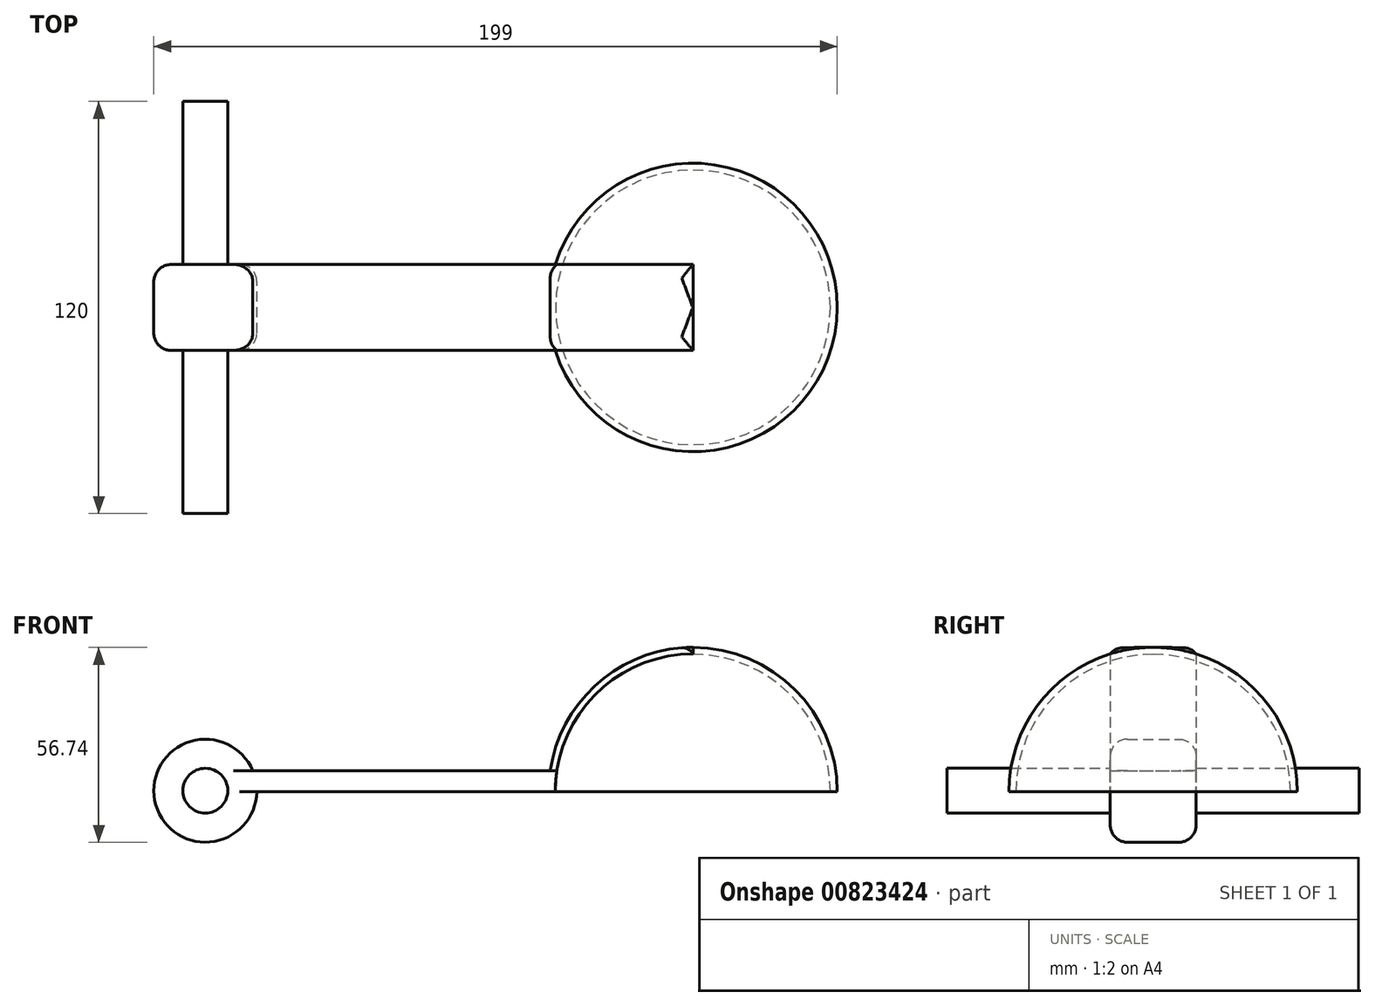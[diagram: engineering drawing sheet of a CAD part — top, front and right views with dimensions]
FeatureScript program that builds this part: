
annotation { "Feature Type Name" : "Feature", "Feature Type Description" : "" }
export const myFeature = defineFeature(function(context is Context, id is Id, definition is map)
    precondition{}
    {
        {
            var Q0;
            Q0=qCreatedBy(makeId("Front.planeOp"),FACE);
            var sketch = newSketch(context, id + "F0", { "sketchPlane" : qUnion([Q0])});
            skLineSegment(sketch, "E0", {"start": v(-42, 0) * mm, "end": v(-40, 0) * mm});
            skLineSegment(sketch, "E1", {"start": v(0, 0) * mm, "end": v(0, 40) * mm});
            skArc(sketch, "E2", {"start": v(-40, 0) * mm, "mid": v(-28.28, 28.28) * mm, "end": v(0, 40) * mm});
            skArc(sketch, "E3.0", {"start": v(-42, 0) * mm, "mid": v(-29.7, 29.7) * mm, "end": v(0, 42) * mm});
            skLineSegment(sketch, "E4", {"start": v(0, 42) * mm, "end": v(0, 40) * mm});
            skPoint(sketch, "E5", {"position": v(0, 20) * mm});
            skPoint(sketch, "E6", {"position": v(-36.93, 20) * mm});
            skPoint(sketch, "E7", {"position": v(-46.93, 20) * mm});
            skArc(sketch, "E8", {"start": v(-36.93, 20) * mm, "mid": v(-36.11, 21.44) * mm, "end": v(-35.24, 22.85) * mm});
            skLineSegment(sketch, "E9", {"start": v(-42, 0) * mm, "end": v(-142, 0) * mm});
            skCircle(sketch, "E10", {"center": v(-142, 0.26) * mm, "radius": 15 * mm});
            skLineSegment(sketch, "E11", {"start": v(-142, 6.07) * mm, "end": v(-41.56, 6.07) * mm});
            skCircle(sketch, "E12", {"center": v(-142, 0.26) * mm, "radius": 6.52 * mm});
            skSolve(sketch);
        }
        {
            var Q0;
            Q0=makeQuery(id+"F0.imprint","IMPRINT",FACE,{"disambiguationData":[TD([[makeQuery(id+"F0.imprint","IMPRINT",EDGE,{"derivedFrom":sQuery(id+"F0.wireOp",EDGE,"E0")}),1.0]])]});
            var Q1;
            Q1=sQuery(id+"F0.wireOp",EDGE,"E1");
            revolve(context, id + "F1", {"entities" : qUnion([Q0]), "axis" : qUnion([Q1]), "revolveType" : RevolveType.FULL, "surfaceOperationType" : NewSurfaceOperationType.NEW});
        }
        {
            var Q0;
            Q0 = qSketchRegion(id + "F0", true);
            extrude(context, id + "F2", {"entities" : qUnion([Q0]), "operationType" : NewBodyOperationType.ADD, "endBound" : BoundingType.SYMMETRIC, "depth" : 25 * mm, "offsetDistance" : 25 * mm});
        }
        {
            var Q0;
            {var subQ0=sQuery(id+"F0.wireOp",EDGE,"E12");var subQ1=makeQuery(id+"F0.imprint","INTERSECT",VERTEX,{"derivedFrom":[sQuery(id+"F0.wireOp",EDGE,"E9"),subQ0]});Q0=makeQuery(id+"F0.imprint","IMPRINT",FACE,{"disambiguationData":[TD([[makeQuery(id+"F0.imprint","IMPRINT",EDGE,{"disambiguationData":[TD([[subQ1,1.0]])],"derivedFrom":subQ0}),1.0]])]});}
            extrude(context, id + "F3", {"entities" : qUnion([Q0]), "operationType" : NewBodyOperationType.ADD, "endBound" : BoundingType.SYMMETRIC, "depth" : 120 * mm, "offsetDistance" : 25 * mm});
        }
        {
            var Q0;
            Q0=makeQuery(id+"F2.opExtrude","CAP_EDGE",EDGE,{"disambiguationData":[OSD([sQuery(id+"F0.wireOp",EDGE,"E10")])],"isStart":true});
            var Q1;
            Q1=makeQuery(id+"F2.opExtrude","CAP_EDGE",EDGE,{"disambiguationData":[OSD([sQuery(id+"F0.wireOp",EDGE,"E10")])],"isStart":false});
            fillet(context, id + "F4", {"entities" : qUnion([Q0, Q1]), "radius" : 5 * mm, "tangentPropagation" : true, "allowEdgeOverflow" : false});
        }
        {
            var Q0;
            Q0=makeQuery(id+"F2.opExtrude","CAP_EDGE",EDGE,{"disambiguationData":[OSD([sQuery(id+"F0.wireOp",EDGE,"E3.0"),sQuery(id+"F0.wireOp",EDGE,"E8")])],"isStart":false});
            var Q1;
            Q1=makeQuery(id+"F2.opExtrude","CAP_EDGE",EDGE,{"disambiguationData":[OSD([sQuery(id+"F0.wireOp",EDGE,"E3.0"),sQuery(id+"F0.wireOp",EDGE,"E8")])],"isStart":true});
            var Q2;
            {var subQ0=sQuery(id+"F0.wireOp",EDGE,"E8");var subQ1=sQuery(id+"F0.wireOp",EDGE,"E3.0");var subQ2=sQuery(id+"F0.wireOp",EDGE,"E4");Q2=makeQuery(id+"F2.boolean.opBoolean","SPLIT",EDGE,{"disambiguationData":[TD([makeQuery(id+"F2.opExtrude","CAP_FACE",FACE,{"disambiguationData":[OSD([sQuery(id+"F0.wireOp",EDGE,"E0"),sQuery(id+"F0.wireOp",EDGE,"E2"),subQ1,subQ2,subQ0,sQuery(id+"F0.wireOp",EDGE,"E9"),sQuery(id+"F0.wireOp",EDGE,"E10"),sQuery(id+"F0.wireOp",EDGE,"E11"),sQuery(id+"F0.wireOp",EDGE,"E12")])],"isStart":false})])],"derivedFrom":makeQuery(id+"F2.opExtrude","SWEPT_EDGE",EDGE,{"disambiguationData":[OSD([subQ1,subQ2])]})});}
            fillet(context, id + "F5", {"entities" : qUnion([Q0, Q1, Q2]), "radius" : 5 * mm, "tangentPropagation" : true, "allowEdgeOverflow" : false});
        }
    });
